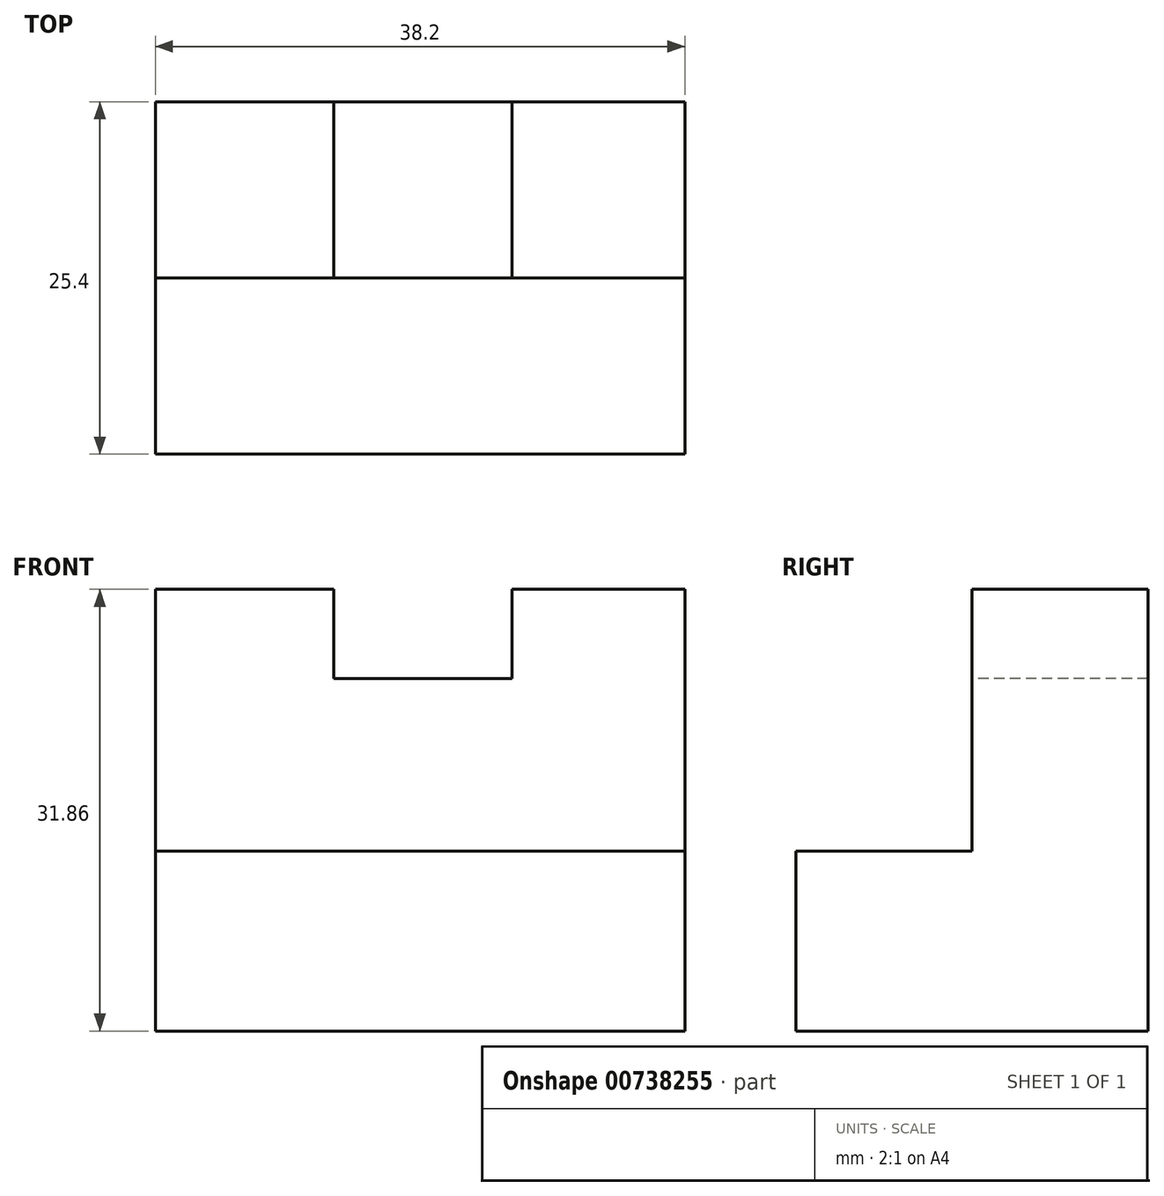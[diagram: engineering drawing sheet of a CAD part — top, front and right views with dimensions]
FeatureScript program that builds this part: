
annotation { "Feature Type Name" : "Feature", "Feature Type Description" : "" }
export const myFeature = defineFeature(function(context is Context, id is Id, definition is map)
    precondition{}
    {
        {
            var Q0;
            Q0=qCreatedBy(makeId("Front.planeOp"),FACE);
            var sketch = newSketch(context, id + "F0", { "sketchPlane" : qUnion([Q0])});
            skLineSegment(sketch, "E0", {"start": v(-50.56, 0) * mm, "end": v(-12.36, 0) * mm});
            skLineSegment(sketch, "E1", {"start": v(-12.36, 0) * mm, "end": v(-12.36, 31.86) * mm});
            skLineSegment(sketch, "E2", {"start": v(-50.56, 0) * mm, "end": v(-50.56, 31.86) * mm});
            skLineSegment(sketch, "E3", {"start": v(-50.56, 31.86) * mm, "end": v(-12.36, 31.86) * mm});
            skSolve(sketch);
        }
        {
            var Q0;
            Q0 = qSketchRegion(id + "F0", true);
            extrude(context, id + "F1", {"entities" : qUnion([Q0]), "depth" : 25.4 * mm, "offsetDistance" : 25.4 * mm});
        }
        {
            var Q0;
            Q0=makeQuery(id+"F1.opExtrude","CAP_FACE",FACE,{"disambiguationData":[OSD([sQuery(id+"F0.wireOp",EDGE,"E0"),sQuery(id+"F0.wireOp",EDGE,"E1"),sQuery(id+"F0.wireOp",EDGE,"E2"),sQuery(id+"F0.wireOp",EDGE,"E3")])],"isStart":false});
            var sketch = newSketch(context, id + "F2", { "sketchPlane" : qUnion([Q0])});
            skLineSegment(sketch, "E4", {"start": v(-50.56, 0) * mm, "end": v(-50.56, 12.97) * mm});
            skLineSegment(sketch, "E5", {"start": v(-50.56, 12.97) * mm, "end": v(-12.36, 12.97) * mm});
            skLineSegment(sketch, "E6", {"start": v(-50.56, 6.48) * mm, "end": v(-50.56, 8.74) * mm});
            skSolve(sketch);
        }
        {
            var Q0;
            {var subQ0=sQuery(id+"F2.wireOp",EDGE,"E5");Q0=makeQuery(id+"F2.imprint","IMPRINT",FACE,{"disambiguationData":[TD([[makeQuery(id+"F2.imprint","IMPRINT",EDGE,{"derivedFrom":subQ0}),1.0]])]});}
            extrude(context, id + "F3", {"entities" : qUnion([Q0]), "operationType" : NewBodyOperationType.REMOVE, "oppositeDirection" : true, "depth" : 12.7 * mm, "offsetDistance" : 25.4 * mm});
        }
        {
            var Q0;
            Q0=makeQuery(id+"F3.boolean.opBoolean","COPY",FACE,{"derivedFrom":makeQuery(id+"F3.opExtrude","CAP_FACE",FACE,{"disambiguationData":[OSD([sQuery(id+"F0.wireOp",EDGE,"E1"),sQuery(id+"F0.wireOp",EDGE,"E2"),sQuery(id+"F0.wireOp",EDGE,"E3"),sQuery(id+"F2.wireOp",EDGE,"E5")])],"isStart":false})});
            var sketch = newSketch(context, id + "F4", { "sketchPlane" : qUnion([Q0])});
            skLineSegment(sketch, "E7", {"start": v(-50.56, 31.86) * mm, "end": v(-37.7, 31.86) * mm});
            skLineSegment(sketch, "E8", {"start": v(-37.7, 31.86) * mm, "end": v(-37.7, 25.43) * mm});
            skLineSegment(sketch, "E9", {"start": v(-37.7, 25.43) * mm, "end": v(-24.83, 25.43) * mm});
            skLineSegment(sketch, "E10", {"start": v(-24.83, 25.43) * mm, "end": v(-24.83, 31.86) * mm});
            skSolve(sketch);
        }
        {
            var Q0;
            {var subQ0=sQuery(id+"F4.wireOp",EDGE,"E8");Q0=makeQuery(id+"F4.imprint","IMPRINT",FACE,{"disambiguationData":[TD([[makeQuery(id+"F4.imprint","IMPRINT",EDGE,{"derivedFrom":subQ0}),1.0]])]});}
            extrude(context, id + "F5", {"entities" : qUnion([Q0]), "operationType" : NewBodyOperationType.REMOVE, "endBound" : BoundingType.THROUGH_ALL, "oppositeDirection" : true, "depth" : 25.4 * mm, "offsetDistance" : 25.4 * mm});
        }
    });
